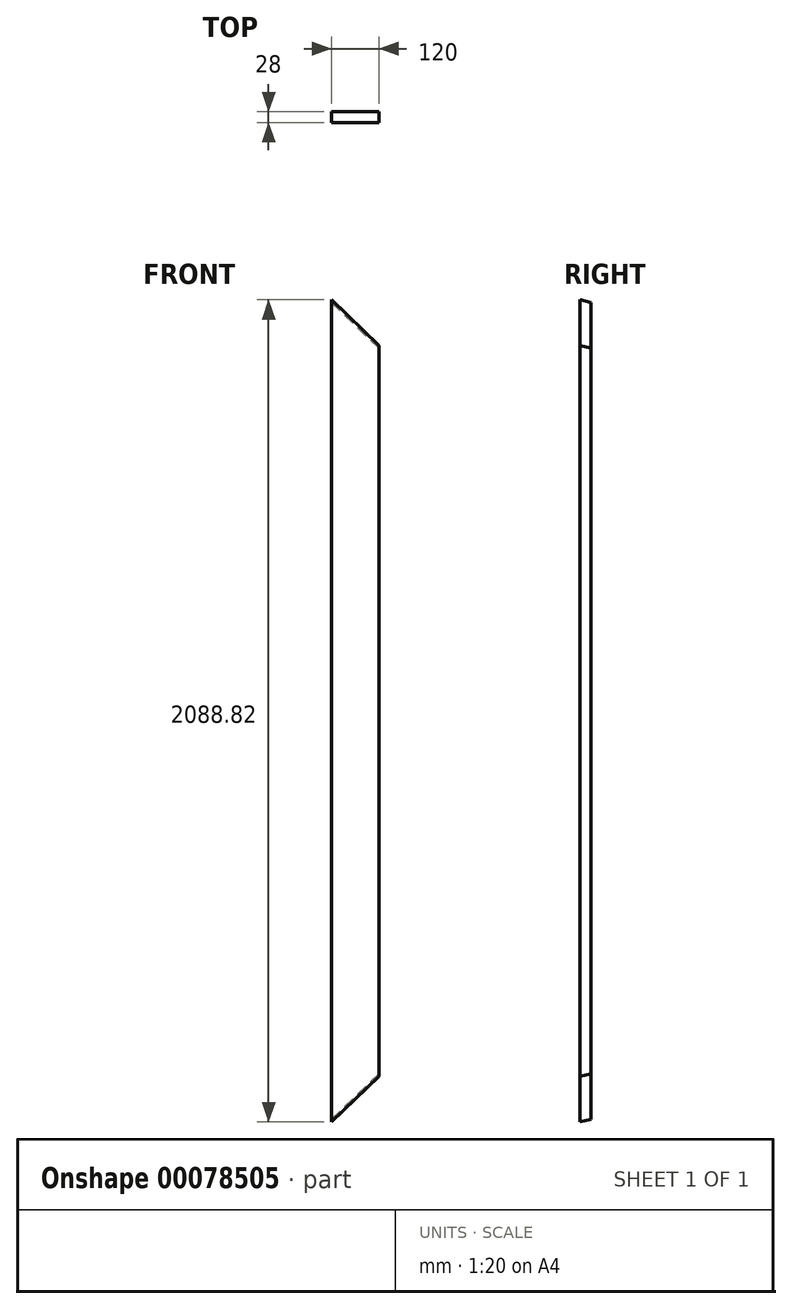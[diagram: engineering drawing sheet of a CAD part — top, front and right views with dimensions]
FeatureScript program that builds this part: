
annotation { "Feature Type Name" : "Feature", "Feature Type Description" : "" }
export const myFeature = defineFeature(function(context is Context, id is Id, definition is map)
    precondition{}
    {
        {
            var Q0;
            Q0=qCreatedBy(makeId("Top.planeOp"),FACE);
            var sketch = newSketch(context, id + "F0", { "sketchPlane" : qUnion([Q0])});
            skLineSegment(sketch, "E0.bottom", {"start": v(60, -14) * mm, "end": v(-60, -14) * mm});
            skLineSegment(sketch, "E0.top", {"start": v(60, 14) * mm, "end": v(-60, 14) * mm});
            skLineSegment(sketch, "E0.left", {"start": v(60, -14) * mm, "end": v(60, 14) * mm});
            skLineSegment(sketch, "E0.right", {"start": v(-60, -14) * mm, "end": v(-60, 14) * mm});
            skPoint(sketch, "E0.middle", {"position": v(0, 0) * mm});
            skSolve(sketch);
        }
        {
            var Q0;
            Q0=makeQuery(id+"F0.imprint","IMPRINT",FACE,{"disambiguationData":[TD([[makeQuery(id+"F0.imprint","IMPRINT",EDGE,{"derivedFrom":sQuery(id+"F0.wireOp",EDGE,"E0.bottom")}),-1.0]])]});
            extrude(context, id + "F1", {"entities" : qUnion([Q0]), "endBound" : BoundingType.SYMMETRIC, "depth" : 2100 * mm});
        }
        {
            var Q0;
            Q0=makeQuery(id+"F1.opExtrude","CAP_EDGE",EDGE,{"disambiguationData":[OSD([sQuery(id+"F0.wireOp",EDGE,"E0.left")])],"isStart":true});
            var Q1;
            Q1=makeQuery(id+"F1.opExtrude","CAP_EDGE",EDGE,{"disambiguationData":[OSD([sQuery(id+"F0.wireOp",EDGE,"E0.left")])],"isStart":false});
            chamfer(context, id + "F2", {"entities" : qUnion([Q0, Q1]), "chamferType" : ChamferType.OFFSET_ANGLE, "width" : 120 * mm, "oppositeDirection" : false, "angle" : 46 * degree, "tangentPropagation" : true});
        }
        {
            var Q0;
            Q0=makeQuery(id+"F2.opChamfer","BLEND_EDGE",EDGE,{"blendedFrom":[makeQuery(id+"F1.opExtrude","CAP_EDGE",EDGE,{"disambiguationData":[OSD([sQuery(id+"F0.wireOp",EDGE,"E0.left")])],"isStart":true}),makeQuery(id+"F1.opExtrude","SWEPT_FACE",FACE,{"disambiguationData":[OSD([sQuery(id+"F0.wireOp",EDGE,"E0.top")])]})],"blendedInto":[makeQuery(id+"F1.opExtrude","SWEPT_FACE",FACE,{"disambiguationData":[OSD([sQuery(id+"F0.wireOp",EDGE,"E0.top")])]})]});
            var Q1;
            Q1=makeQuery(id+"F2.opChamfer","BLEND_EDGE",EDGE,{"blendedFrom":[makeQuery(id+"F1.opExtrude","CAP_EDGE",EDGE,{"disambiguationData":[OSD([sQuery(id+"F0.wireOp",EDGE,"E0.left")])],"isStart":false}),makeQuery(id+"F1.opExtrude","SWEPT_FACE",FACE,{"disambiguationData":[OSD([sQuery(id+"F0.wireOp",EDGE,"E0.top")])]})],"blendedInto":[makeQuery(id+"F1.opExtrude","SWEPT_FACE",FACE,{"disambiguationData":[OSD([sQuery(id+"F0.wireOp",EDGE,"E0.top")])]})]});
            chamfer(context, id + "F3", {"entities" : qUnion([Q0, Q1]), "chamferType" : ChamferType.OFFSET_ANGLE, "width" : 6 * mm, "oppositeDirection" : false, "angle" : 80 * degree, "tangentPropagation" : true});
        }
    });
